# Revit family: Unterlegscheibe VA
name_source: partatom
category: HLS-Bauteile
revit_build: Autodesk Revit 2017 (Build: 20190507_1515(x64)
units: mm (PartAtom-declared; Revit-internal decimal feet)

## family parameters
Arbeitsebenenbasiert = Ja
Beim Laden mit Abzugskörper schneiden = Nein
Bemaßung runder Anschluss = Durchmesser verwenden
Gemeinsam genutzt = Ja
Immer vertikal = Nein
Raumberechnungspunkt = Nein
Teiletyp = Normal

## types (15) — shared parameters
Firma = MEFA Befestigungs- und Montagesysteme GmbH
Vorgabe-Ansicht = 1219 mm

## per-type parameters (varying)
| type | Artikelnummer | D | D0 | EAN | Fabrikat | Gewicht | Gewicht pro Bauteil | Kurztext1 | Kurztext2 | Material | Mengeneinheit | S | vpe |
| Unterlegscheibe  8,4x16x1,6 V2A | 4338108 | 16 mm  [stored 0.0524934 ft] | 8 mm  [stored 0.0262467 ft] | 4250928439161 | MEFA | 0.00 kg | 0.00 kg | Unterlegscheibe EN ISO 7089 V2A | 8,4 x 16 x 1,6 mm | Edelstahl | St | 2 mm  [stored 0.00656168 ft] | 100 St |
| Unterlegscheibe 10,5x20x2,0 V2A | 4338110 | 20 mm  [stored 0.0656168 ft] | 11 mm | 4250928439178 | MEFA | 0.00 kg | 0.00 kg | Unterlegscheibe EN ISO 7089 V2A | 10,5 x 20 x 2 mm | Edelstahl | St | 2 mm  [stored 0.00656168 ft] | 100 St |
| Unterlegscheibe 13,0x24x2,5 V2A | 4338113 | 24 mm  [stored 0.0787402 ft] | 13 mm | 4250928439185 | MEFA | 0.01 kg | 0.01 kg | Unterlegscheibe EN ISO 7089 V2A | 13 x 24 x 2,5 mm | Edelstahl | St | 3 mm  [stored 0.00984252 ft] | 100 St |
| Unterlegscheibe  8,4x25x2,0 V2A | 4338008 | 25 mm  [stored 0.082021 ft] | 8 mm  [stored 0.0262467 ft] | 4250928439123 | MEFA | 0.01 kg | 0.01 kg | Unterlegscheibe EN ISO 7093-1 V2A | 8,4 x 25 x 2 mm | Edelstahl | St | 2 mm  [stored 0.00656168 ft] | 100 St |
| Unterlegscheibe 10,5x30x2,5 V2A | 3228010 | 30 mm  [stored 0.0984252 ft] | 11 mm |  |  | 0.00 kg | 0.00 kg |  |  |  |  | 3 mm  [stored 0.00984252 ft] |  |
| Unterlegscheibe 13,0x37x3,0 V2A | 4338013 | 37 mm  [stored 0.121391 ft] | 13 mm | 4250928439147 | MEFA | 0.02 kg | 0.02 kg | Unterlegscheibe EN ISO 7093-1 V2A | 13 x 37 x 3 mm | Edelstahl | St | 3 mm  [stored 0.00984252 ft] | 100 St |
| Unterlegscheibe 17,0x50x3,0 V2A | 4338017 | 50 mm  [stored 0.164042 ft] | 17 mm | 4250928439154 | MEFA | 0.04 kg | 0.04 kg | Unterlegscheibe EN ISO 7093-1 V2A | 17 x 50 x 3 mm | Edelstahl | St | 3 mm  [stored 0.00984252 ft] | 50 St |
| Unterlegscheibe 10,5x40x3,0 V4A | 43385103 | 40 mm  [stored 0.131234 ft] | 11 mm | 4250928448958 | MEFA | 0.03 kg | 0.03 kg | Unterlegscheibe V4A | 10,5 x 40 x 3 mm | Edelstahl | St | 3 mm  [stored 0.00984252 ft] | 100 St |
| Unterlegscheibe  8,4x16x1,6 V4A | 4338118 | 16 mm  [stored 0.0524934 ft] | 8 mm  [stored 0.0262467 ft] | 4250928439192 | MEFA | 0.00 kg | 0.00 kg | Unterlegscheibe EN ISO 7089 V4A | 8,4 x 16 x 1,6 mm | Edelstahl | St | 2 mm  [stored 0.00656168 ft] | 100 St |
| Unterlegscheibe 10,5x20x2,0 V4A | 4338120 | 20 mm  [stored 0.0656168 ft] | 11 mm | 4250928439208 | MEFA | 0.00 kg | 0.00 kg | Unterlegscheibe EN ISO 7089 V4A | 10,5 x 20 x 2 mm | Edelstahl | St | 2 mm  [stored 0.00656168 ft] | 100 St |
| Unterlegscheibe 13,0x24x2,5 V4A | 4338123 | 24 mm  [stored 0.0787402 ft] | 13 mm | 4250928439215 | MEFA | 0.01 kg | 0.01 kg | Unterlegscheibe EN ISO 7089 V4A | 13 x 24 x 2,5 mm | Edelstahl | St | 3 mm  [stored 0.00984252 ft] | 100 St |
| Unterlegscheibe  8,4x25x2,0 V4A | 4338208 | 25 mm  [stored 0.082021 ft] | 8 mm  [stored 0.0262467 ft] | 4250928439222 | MEFA | 0.01 kg | 0.01 kg | Unterlegscheibe EN ISO 7093-1 V4A | 8,4 x 25 x 2 mm | Edelstahl | St | 2 mm  [stored 0.00656168 ft] | 100 St |
| Unterlegscheibe 10,5x30x2,5 V4A | 4338210 | 30 mm  [stored 0.0984252 ft] | 11 mm | 4250928439239 | MEFA | 0.01 kg | 0.01 kg | Unterlegscheibe EN ISO 7093-1 V4A | 10,5 x 30 x 2,5 mm | Edelstahl | St | 3 mm  [stored 0.00984252 ft] | 100 St |
| Unterlegscheibe 13,0x37x3,0 V4A | 4338213 | 37 mm  [stored 0.121391 ft] | 13 mm | 4250928439246 | MEFA | 0.02 kg | 0.02 kg | Unterlegscheibe EN ISO 7093-1 V4A | 13 x 37 x 3 mm | Edelstahl | St | 3 mm  [stored 0.00984252 ft] | 100 St |
| Unterlegscheibe 17,0x50x3,0 V4A | 4338217 | 50 mm  [stored 0.164042 ft] | 17 mm | 4250928439253 | MEFA | 0.04 kg | 0.04 kg | Unterlegscheibe EN ISO 7093-1 V4A | 17 x 50 x 3 mm | Edelstahl | St | 3 mm  [stored 0.00984252 ft] | 50 St |

note: [stored X ft] marks values corroborated as IEEE doubles in the binary element streams (Revit-internal decimal feet)
